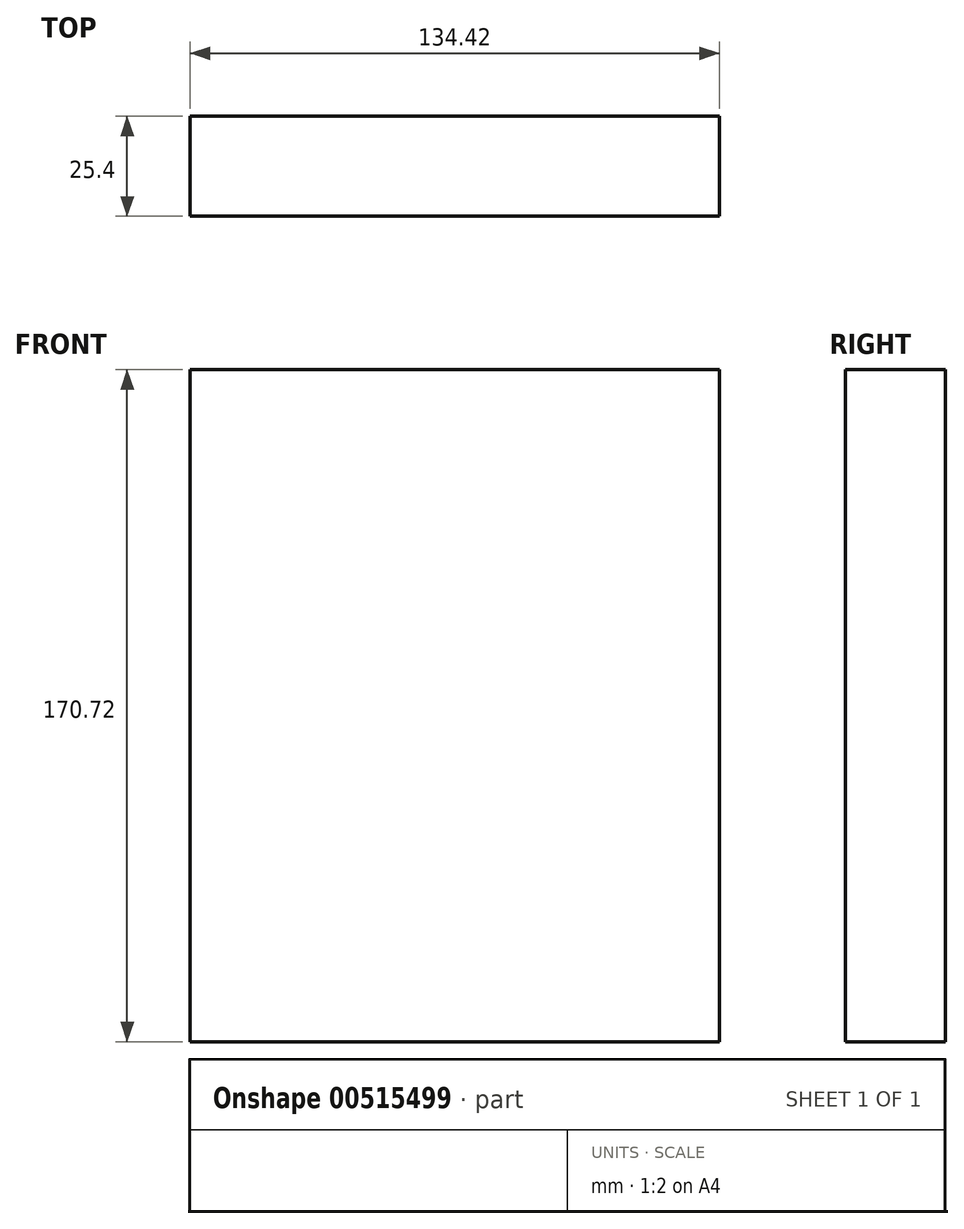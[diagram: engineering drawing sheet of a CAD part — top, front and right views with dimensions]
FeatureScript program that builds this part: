
annotation { "Feature Type Name" : "Feature", "Feature Type Description" : "" }
export const myFeature = defineFeature(function(context is Context, id is Id, definition is map)
    precondition{}
    {
        {
            var Q0;
            Q0=qCreatedBy(makeId("Front.planeOp"),FACE);
            var sketch = newSketch(context, id + "F0", { "sketchPlane" : qUnion([Q0])});
            skLineSegment(sketch, "E0.bottom", {"start": v(0, 14.57) * mm, "end": v(-134.42, 14.57) * mm});
            skLineSegment(sketch, "E0.top", {"start": v(0, -156.15) * mm, "end": v(-134.42, -156.15) * mm});
            skLineSegment(sketch, "E0.left", {"start": v(0, 14.57) * mm, "end": v(0, -156.15) * mm});
            skLineSegment(sketch, "E0.right", {"start": v(-134.42, 14.57) * mm, "end": v(-134.42, -156.15) * mm});
            skSolve(sketch);
        }
        {
            var Q0;
            Q0 = qSketchRegion(id + "F0", true);
            extrude(context, id + "F1", {"entities" : qUnion([Q0]), "depth" : 25.4 * mm, "offsetDistance" : 25.4 * mm});
        }
    });
